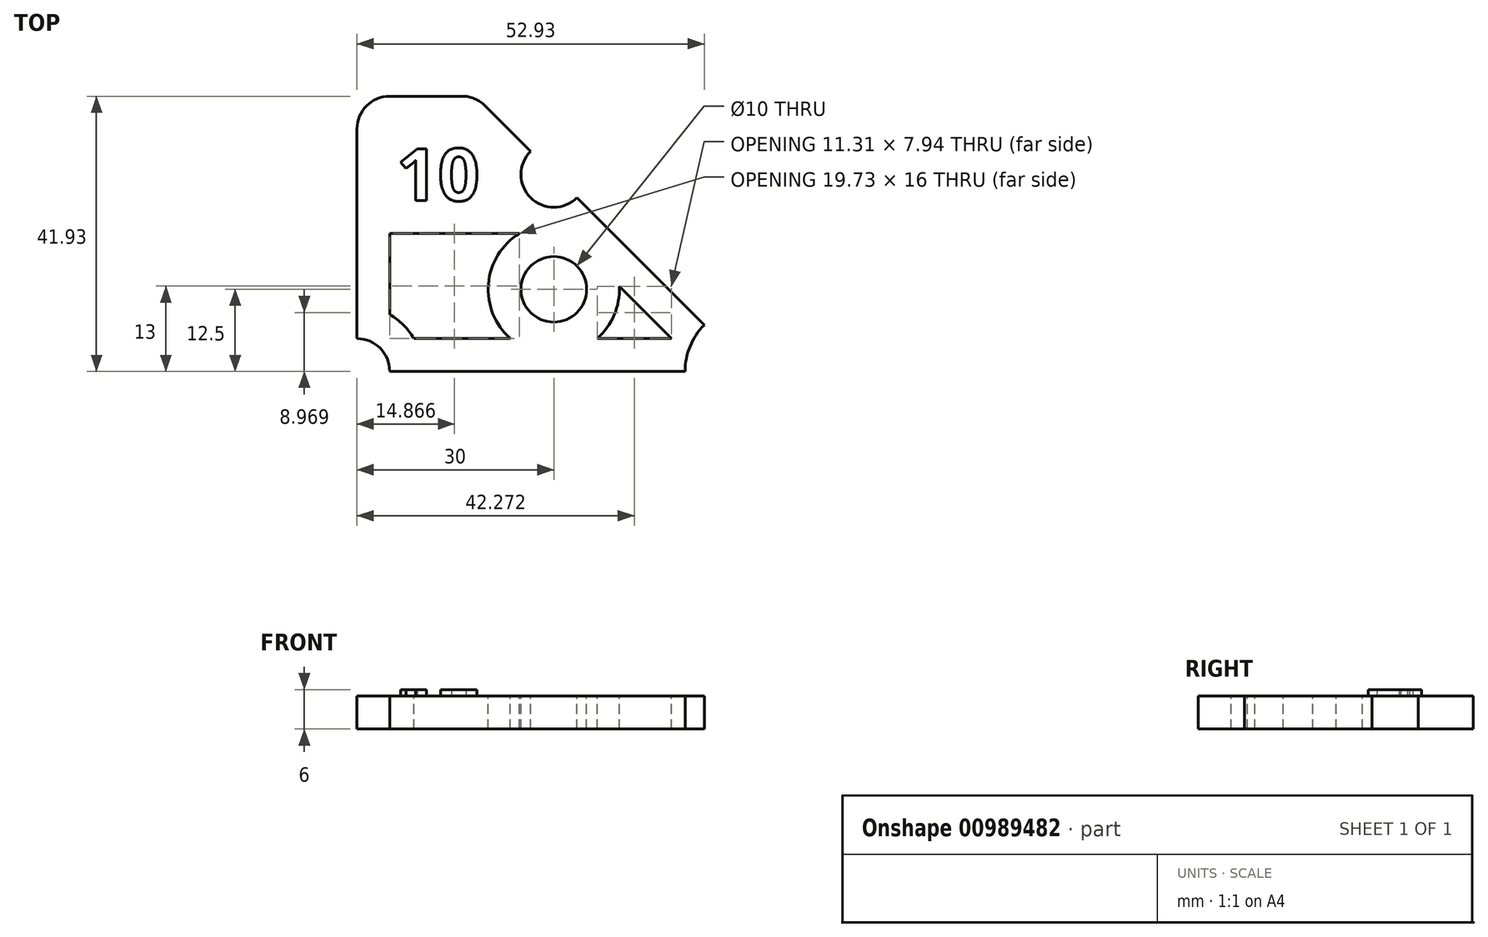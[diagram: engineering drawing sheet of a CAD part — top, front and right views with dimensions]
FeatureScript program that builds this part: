
annotation { "Feature Type Name" : "Feature", "Feature Type Description" : "" }
export const myFeature = defineFeature(function(context is Context, id is Id, definition is map)
    precondition{}
    {
        {
            var Q0;
            Q0=qCreatedBy(makeId("Top.planeOp"),FACE);
            var sketch = newSketch(context, id + "F0", { "sketchPlane" : qUnion([Q0])});
            skLineSegment(sketch, "E0", {"start": v(-30, 30) * mm, "end": v(-30, -30) * mm});
            skLineSegment(sketch, "E1", {"start": v(-30, -30) * mm, "end": v(30, -30) * mm});
            skLineSegment(sketch, "E2", {"start": v(30, -30) * mm, "end": v(-30, 30) * mm});
            skPoint(sketch, "E3", {"position": v(0, 0) * mm});
            skCircle(sketch, "E4", {"center": v(-30, -30) * mm, "radius": 5 * mm});
            skCircle(sketch, "E5", {"center": v(30, -30) * mm, "radius": 5 * mm});
            skCircle(sketch, "E6", {"center": v(0, 0) * mm, "radius": 5 * mm});
            skLineSegment(sketch, "E7", {"start": v(0, 0) * mm, "end": v(-30, -30) * mm, "construction": true});
            skCircle(sketch, "E8", {"center": v(0, -17.5) * mm, "radius": 5 * mm});
            skLineSegment(sketch, "E9", {"start": v(0, -5) * mm, "end": v(0, -30) * mm, "construction": true});
            skPoint(sketch, "E9.startSnap0", {"position": v(0, -30) * mm});
            skLineSegment(sketch, "E10", {"start": v(-5, 5) * mm, "end": v(-5, -4.06) * mm, "construction": true});
            skLineSegment(sketch, "E11", {"start": v(-5, 0) * mm, "end": v(-30, 0) * mm, "construction": true});
            skText(sketch, "E12", { "text": "10", "fontName": "OpenSans-Bold.ttf"});
            skPoint(sketch, "E13", {"position": v(-17.5, 0) * mm});
            skLineSegment(sketch, "E14", {"start": v(-25, 11.93) * mm, "end": v(-14, 11.93) * mm});
            skArc(sketch, "E15", {"start": v(-10.46, 10.46) * mm, "mid": v(-12.09, 11.55) * mm, "end": v(-14, 11.93) * mm});
            skArc(sketch, "E16", {"start": v(-25, 11.93) * mm, "mid": v(-28.54, 10.46) * mm, "end": v(-30, 6.93) * mm});
            skArc(sketch, "E17.0", {"start": v(-30, -20) * mm, "mid": v(-37.07, -37.07) * mm, "end": v(-20, -30) * mm});
            skLineSegment(sketch, "E18", {"start": v(-25, -21.34) * mm, "end": v(-25, -9) * mm});
            skLineSegment(sketch, "E19", {"start": v(-25, -9) * mm, "end": v(-5, -9) * mm});
            skLineSegment(sketch, "E20", {"start": v(-5, -9) * mm, "end": v(-5, -25) * mm});
            skLineSegment(sketch, "E21", {"start": v(-5, -25) * mm, "end": v(-21.34, -25) * mm});
            skArc(sketch, "E22.0", {"start": v(-5.27, -9) * mm, "mid": v(-9.96, -16.66) * mm, "end": v(-6.61, -25) * mm});
            skArc(sketch, "E23.trimOffspring", {"start": v(-21.34, -25) * mm, "mid": v(-22.93, -22.93) * mm, "end": v(-25, -21.34) * mm});
            skArc(sketch, "E24.0", {"start": v(22.93, -22.93) * mm, "mid": v(20.76, -26.17) * mm, "end": v(20, -30) * mm});
            skLineSegment(sketch, "E25", {"start": v(5, -12.07) * mm, "end": v(20.34, -27.41) * mm});
            skLineSegment(sketch, "E26", {"start": v(5, -25) * mm, "end": v(21.34, -25) * mm});
            skLineSegment(sketch, "E27", {"start": v(5, -12.07) * mm, "end": v(5, -25) * mm});
            skArc(sketch, "E28.trimOffspring", {"start": v(6.61, -25) * mm, "mid": v(9.2, -21.41) * mm, "end": v(10, -17.06) * mm});
            const initialGuessF0  = {"E12": [-0.024, -0.004, 1, 0, 0.008]};
            skSetInitialGuess(sketch, initialGuessF0);
            skSolve(sketch);
        }
        {
            var Q0;
            Q0=makeQuery(id+"F0.imprint","IMPRINT",FACE,{"disambiguationData":[TD([[makeQuery(id+"F0.imprint","IMPRINT",EDGE,{"derivedFrom":sQuery(id+"F0.wireOp",EDGE,"E12.sketch_text.stroke-0")}),1.0]])]});
            var Q1;
            {var subQ3=sQuery(id+"F0.wireOp",EDGE,"E22.0");Q1=makeQuery(id+"F0.imprint","IMPRINT",FACE,{"disambiguationData":[TD([[makeQuery(id+"F0.imprint","IMPRINT",EDGE,{"derivedFrom":subQ3}),1.0]])]});}
            var Q2;
            {var subQ6=sQuery(id+"F0.wireOp",EDGE,"E28.trimOffspring");Q2=makeQuery(id+"F0.imprint","IMPRINT",FACE,{"disambiguationData":[TD([[makeQuery(id+"F0.imprint","IMPRINT",EDGE,{"derivedFrom":subQ6}),1.0]])]});}
            var Q3;
            {var subQ0=sQuery(id+"F0.wireOp",EDGE,"E25");var subQ1=sQuery(id+"F0.wireOp",EDGE,"E24.0");var subQ2=makeQuery(id+"F0.imprint","INTERSECT",VERTEX,{"derivedFrom":[subQ1,subQ0]});Q3=makeQuery(id+"F0.imprint","IMPRINT",FACE,{"disambiguationData":[TD([[makeQuery(id+"F0.imprint","IMPRINT",EDGE,{"disambiguationData":[TD([[subQ2,1.0]])],"derivedFrom":subQ1}),-1.0]])]});}
            var Q4;
            Q4=makeQuery(id+"F0.imprint","IMPRINT",FACE,{"disambiguationData":[TD([[makeQuery(id+"F0.imprint","IMPRINT",EDGE,{"derivedFrom":sQuery(id+"F0.wireOp",EDGE,"E12.sketch_text.stroke-0")}),-1.0]])]});
            var Q5;
            Q5=makeQuery(id+"F0.imprint","IMPRINT",FACE,{"disambiguationData":[TD([[makeQuery(id+"F0.imprint","IMPRINT",EDGE,{"derivedFrom":sQuery(id+"F0.wireOp",EDGE,"E12.sketch_text.stroke-10")}),-1.0]])]});
            var Q6;
            Q6=makeQuery(id+"F0.imprint","IMPRINT",FACE,{"disambiguationData":[TD([[makeQuery(id+"F0.imprint","IMPRINT",EDGE,{"derivedFrom":sQuery(id+"F0.wireOp",EDGE,"E12.sketch_text.stroke-18")}),1.0]])]});
            extrude(context, id + "F1", {"entities" : qUnion([Q0, Q1, Q2, Q3, Q4, Q5, Q6]), "oppositeDirection" : true, "depth" : 5 * mm, "offsetDistance" : 25 * mm});
        }
        {
            var Q0;
            Q0=makeQuery(id+"F0.imprint","IMPRINT",FACE,{"disambiguationData":[TD([[makeQuery(id+"F0.imprint","IMPRINT",EDGE,{"derivedFrom":sQuery(id+"F0.wireOp",EDGE,"E12.sketch_text.stroke-0")}),-1.0]])]});
            var Q1;
            Q1=makeQuery(id+"F0.imprint","IMPRINT",FACE,{"disambiguationData":[TD([[makeQuery(id+"F0.imprint","IMPRINT",EDGE,{"derivedFrom":sQuery(id+"F0.wireOp",EDGE,"E12.sketch_text.stroke-10")}),-1.0]])]});
            extrude(context, id + "F2", {"entities" : qUnion([Q0, Q1]), "operationType" : NewBodyOperationType.ADD, "depth" : 1 * mm, "offsetDistance" : 25 * mm});
        }
    });
